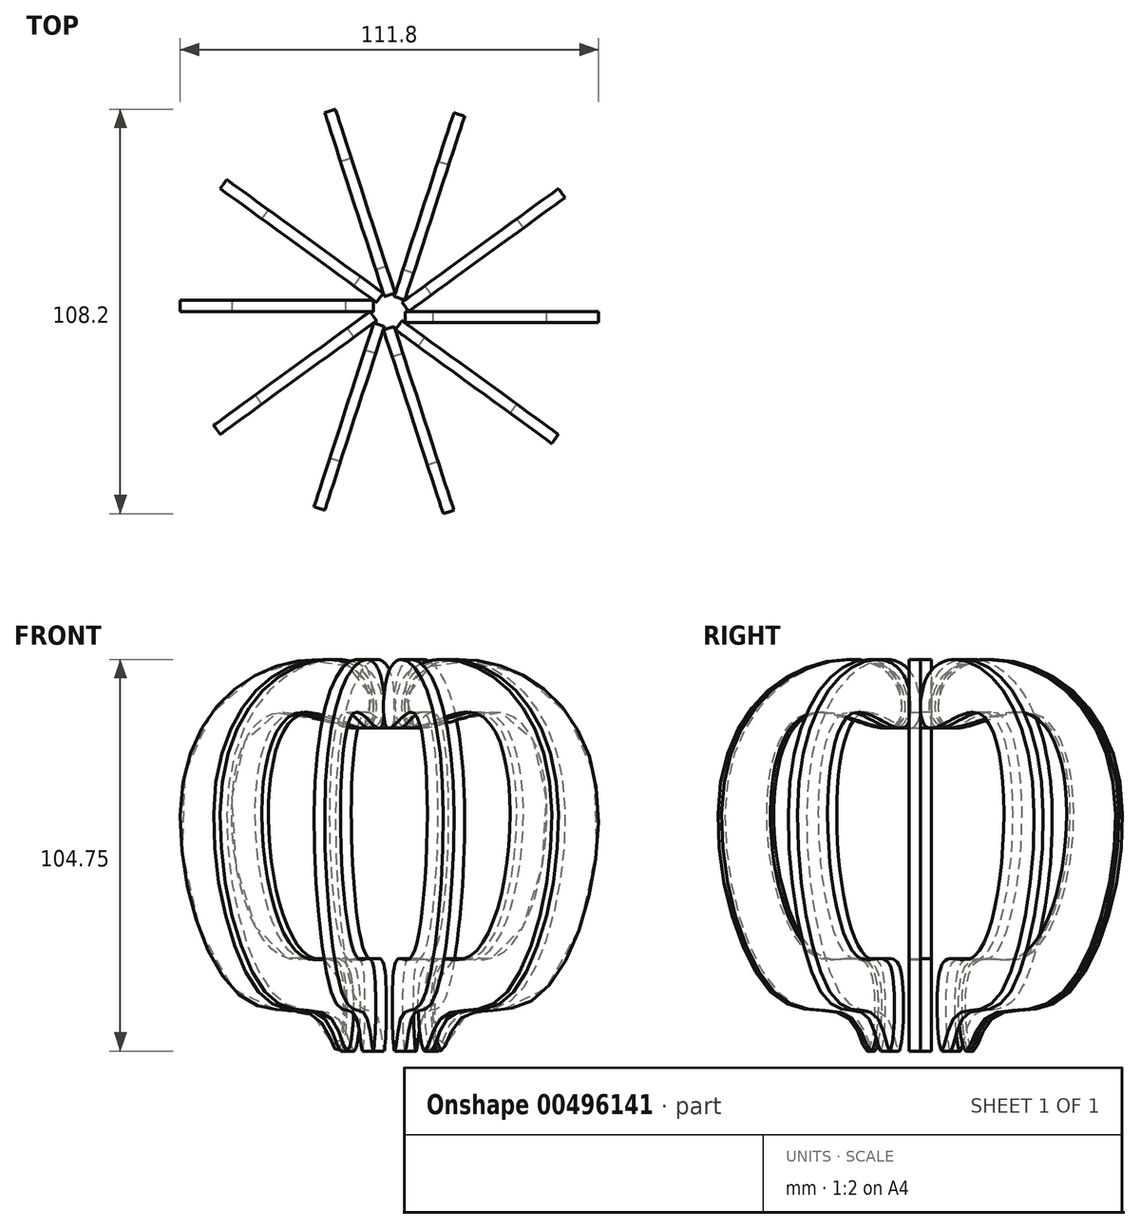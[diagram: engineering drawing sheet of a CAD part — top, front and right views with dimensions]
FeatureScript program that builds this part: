
annotation { "Feature Type Name" : "Feature", "Feature Type Description" : "" }
export const myFeature = defineFeature(function(context is Context, id is Id, definition is map)
    precondition{}
    {
        {
            var Q0;
            Q0=qCreatedBy(makeId("Front.planeOp"),FACE);
            var sketch = newSketch(context, id + "F0", { "sketchPlane" : qUnion([Q0])});
            skFitSpline(sketch, "E0", {"points": [v(6.64, 47.2) * mm, v(6.64, 59.78) * mm, v(29.41, 63.57) * mm, v(55.03, 32.97) * mm, v(38.19, -26.1) * mm, v(18.98, -31.07) * mm, v(13.76, -39.61) * mm, v(13.76, -16.84) * mm, v(27.75, -14.7) * mm, v(42.1, 20.87) * mm, v(30.34, 50.8) * mm, v(6.64, 47.2) * mm]});
            skLineSegment(sketch, "E1", {"start": v(0, 0) * mm, "end": v(0, 68.08) * mm, "construction": true});
            skLineSegment(sketch, "E2", {"start": v(0, 0) * mm, "end": v(0, -52.18) * mm, "construction": true});
            skSolve(sketch);
        }
        {
            var Q0;
            Q0=makeQuery(id+"F0.imprint","IMPRINT",FACE,{"disambiguationData":[TD([[makeQuery(id+"F0.imprint","IMPRINT",EDGE,{"derivedFrom":sQuery(id+"F0.wireOp",EDGE,"E0")}),-1.0]])]});
            extrude(context, id + "F1", {"entities" : qUnion([Q0]), "depth" : 3 * mm});
        }
        {
            var Q0;
            Q0=makeQuery(id+"F1.opExtrude","SWEPT_BODY",BODY,{"disambiguationData":[OSD([sQuery(id+"F0.wireOp",EDGE,"E0")])]});
            var Q1;
            Q1=sQuery(id+"F0.wireOp",EDGE,"E1");
            circularPattern(context, id + "F2", {"operationType" : NewBodyOperationType.ADD, "entities" : qUnion([Q0]), "axis" : qUnion([Q1]), "angle" : 360 * degree, "instanceCount" : 10, "oppositeDirection" : true, "equalSpace" : true});
        }
    });
